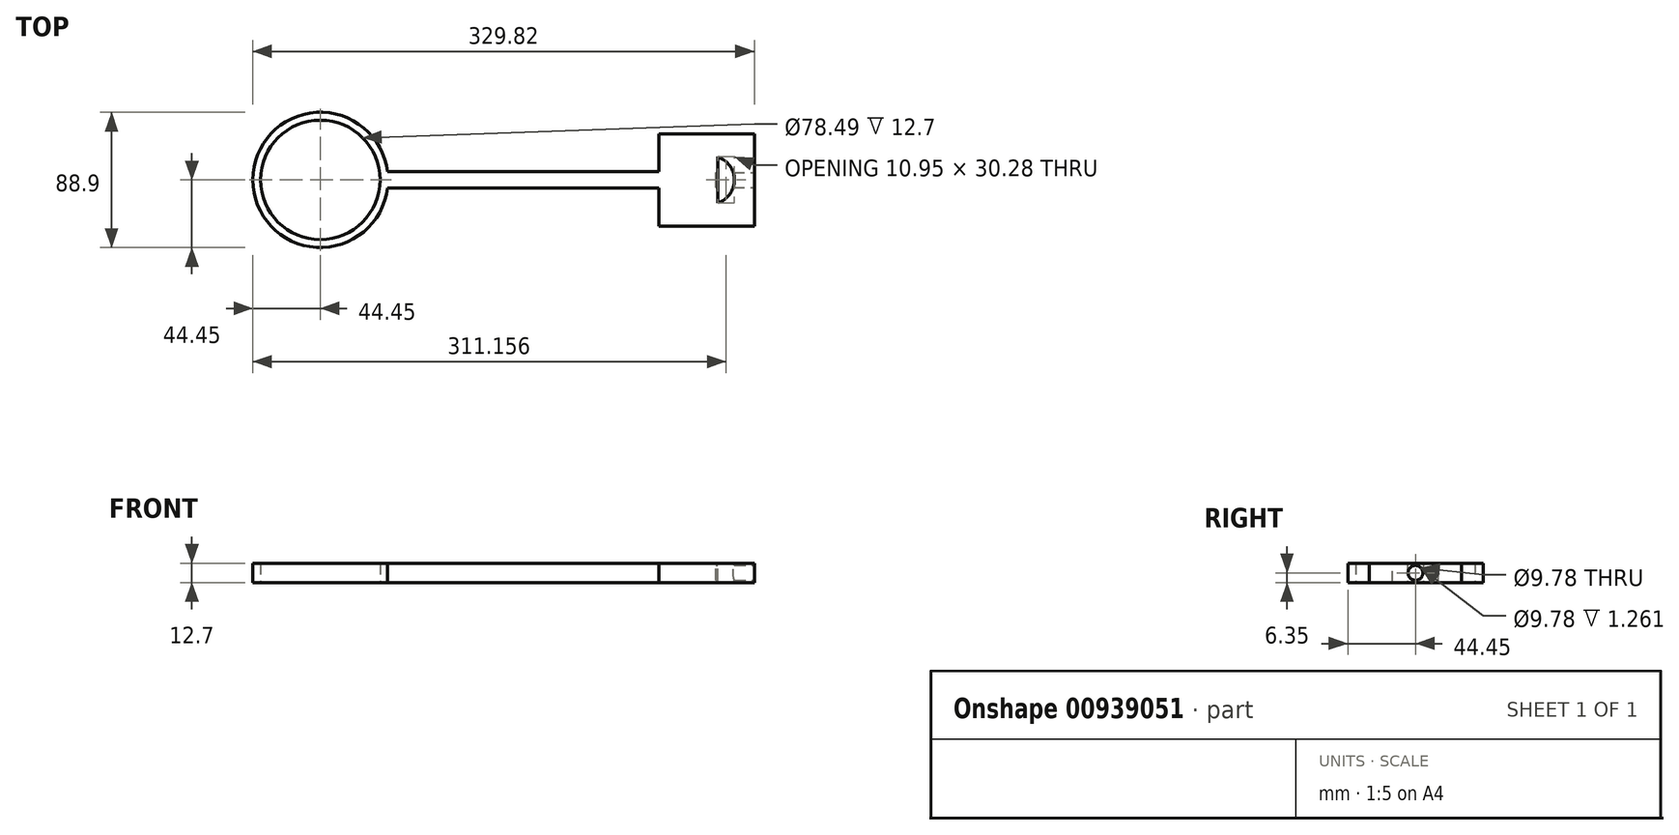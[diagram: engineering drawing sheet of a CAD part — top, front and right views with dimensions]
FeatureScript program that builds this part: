
annotation { "Feature Type Name" : "Feature", "Feature Type Description" : "" }
export const myFeature = defineFeature(function(context is Context, id is Id, definition is map)
    precondition{}
    {
        {
            var Q0;
            Q0=qCreatedBy(makeId("Top.planeOp"),FACE);
            var sketch = newSketch(context, id + "F0", { "sketchPlane" : qUnion([Q0])});
            skLineSegment(sketch, "E0", {"start": v(0, 0) * mm, "end": v(254, 0) * mm});
            skCircle(sketch, "E1", {"center": v(0, 0) * mm, "radius": 39.24 * mm});
            skCircle(sketch, "E2", {"center": v(0, 0) * mm, "radius": 44.45 * mm});
            skLineSegment(sketch, "E3.bottom", {"start": v(285.37, 30.32) * mm, "end": v(222.63, 30.32) * mm});
            skLineSegment(sketch, "E3.top", {"start": v(285.37, -30.32) * mm, "end": v(222.63, -30.32) * mm});
            skLineSegment(sketch, "E3.left", {"start": v(285.37, 30.32) * mm, "end": v(285.37, -30.32) * mm});
            skLineSegment(sketch, "E3.right", {"start": v(222.63, 30.32) * mm, "end": v(222.63, -30.32) * mm});
            skPoint(sketch, "E3.middle", {"position": v(254, 0) * mm});
            skLineSegment(sketch, "E4.bottom", {"start": v(222.63, -5.3) * mm, "end": v(-144.15, -5.3) * mm});
            skLineSegment(sketch, "E4.top", {"start": v(222.63, 5.3) * mm, "end": v(-144.15, 5.3) * mm});
            skLineSegment(sketch, "E4.left", {"start": v(222.63, -5.3) * mm, "end": v(222.63, 5.3) * mm});
            skLineSegment(sketch, "E4.right", {"start": v(-144.15, -5.3) * mm, "end": v(-144.15, 5.3) * mm});
            skPoint(sketch, "E4.middle", {"position": v(39.24, 0) * mm});
            skSolve(sketch);
        }
        {
            var Q0;
            {var subQ3=sQuery(id+"F0.wireOp",EDGE,"E3.bottom");Q0=makeQuery(id+"F0.imprint","IMPRINT",FACE,{"disambiguationData":[TD([[makeQuery(id+"F0.imprint","IMPRINT",EDGE,{"derivedFrom":subQ3}),1.0]])]});}
            var Q1;
            {var subQ0=sQuery(id+"F0.wireOp",EDGE,"E2");var subQ1=sQuery(id+"F0.wireOp",EDGE,"E0");var subQ2=makeQuery(id+"F0.imprint","INTERSECT",VERTEX,{"derivedFrom":[subQ1,subQ0]});Q1=makeQuery(id+"F0.imprint","IMPRINT",FACE,{"disambiguationData":[TD([[makeQuery(id+"F0.imprint","IMPRINT",EDGE,{"disambiguationData":[TD([[subQ2,-1.0]])],"derivedFrom":subQ1}),1.0]])]});}
            var Q2;
            {var subQ0=sQuery(id+"F0.wireOp",EDGE,"E2");var subQ1=sQuery(id+"F0.wireOp",EDGE,"E0");var subQ2=makeQuery(id+"F0.imprint","INTERSECT",VERTEX,{"derivedFrom":[subQ1,subQ0]});Q2=makeQuery(id+"F0.imprint","IMPRINT",FACE,{"disambiguationData":[TD([[makeQuery(id+"F0.imprint","IMPRINT",EDGE,{"disambiguationData":[TD([[subQ2,-1.0]])],"derivedFrom":subQ1}),-1.0]])]});}
            var Q3;
            {var subQ0=sQuery(id+"F0.wireOp",EDGE,"E4.top");var subQ1=sQuery(id+"F0.wireOp",EDGE,"E1");var subQ2=makeQuery(id+"F0.imprint","INTERSECT",VERTEX,{"disambiguationData":[OD(0.0)],"derivedFrom":[subQ1,subQ0]});Q3=makeQuery(id+"F0.imprint","IMPRINT",FACE,{"disambiguationData":[TD([[makeQuery(id+"F0.imprint","IMPRINT",EDGE,{"disambiguationData":[TD([[subQ2,-1.0]])],"derivedFrom":subQ1}),-1.0]])]});}
            var Q4;
            {var subQ0=sQuery(id+"F0.wireOp",EDGE,"E4.bottom");var subQ1=sQuery(id+"F0.wireOp",EDGE,"E1");var subQ2=makeQuery(id+"F0.imprint","INTERSECT",VERTEX,{"disambiguationData":[OD(0.0)],"derivedFrom":[subQ1,subQ0]});Q4=makeQuery(id+"F0.imprint","IMPRINT",FACE,{"disambiguationData":[TD([[makeQuery(id+"F0.imprint","IMPRINT",EDGE,{"disambiguationData":[TD([[subQ2,1.0]])],"derivedFrom":subQ1}),-1.0]])]});}
            var Q5;
            {var subQ0=sQuery(id+"F0.wireOp",EDGE,"E2");var subQ1=sQuery(id+"F0.wireOp",EDGE,"E0");var subQ2=makeQuery(id+"F0.imprint","INTERSECT",VERTEX,{"derivedFrom":[subQ1,subQ0]});Q5=makeQuery(id+"F0.imprint","IMPRINT",FACE,{"disambiguationData":[TD([[makeQuery(id+"F0.imprint","IMPRINT",EDGE,{"disambiguationData":[TD([[subQ2,1.0]])],"derivedFrom":subQ1}),1.0]])]});}
            var Q6;
            {var subQ0=sQuery(id+"F0.wireOp",EDGE,"E2");var subQ1=sQuery(id+"F0.wireOp",EDGE,"E0");var subQ2=makeQuery(id+"F0.imprint","INTERSECT",VERTEX,{"derivedFrom":[subQ1,subQ0]});Q6=makeQuery(id+"F0.imprint","IMPRINT",FACE,{"disambiguationData":[TD([[makeQuery(id+"F0.imprint","IMPRINT",EDGE,{"disambiguationData":[TD([[subQ2,1.0]])],"derivedFrom":subQ1}),-1.0]])]});}
            var Q7;
            {var subQ0=sQuery(id+"F0.wireOp",EDGE,"E4.top");var subQ1=sQuery(id+"F0.wireOp",EDGE,"E1");var subQ2=makeQuery(id+"F0.imprint","INTERSECT",VERTEX,{"disambiguationData":[OD(1.0)],"derivedFrom":[subQ1,subQ0]});Q7=makeQuery(id+"F0.imprint","IMPRINT",FACE,{"disambiguationData":[TD([[makeQuery(id+"F0.imprint","IMPRINT",EDGE,{"disambiguationData":[TD([[subQ2,-1.0]])],"derivedFrom":subQ1}),-1.0]])]});}
            extrude(context, id + "F1", {"entities" : qUnion([Q0, Q1, Q2, Q3, Q4, Q5, Q6, Q7]), "depth" : 12.7 * mm, "offsetDistance" : 25.4 * mm});
        }
        {
            var Q0;
            Q0=makeQuery(id+"F1.opExtrude","CAP_FACE",FACE,{"disambiguationData":[OSD([sQuery(id+"F0.wireOp",EDGE,"E1"),sQuery(id+"F0.wireOp",EDGE,"E2"),sQuery(id+"F0.wireOp",EDGE,"E3.bottom"),sQuery(id+"F0.wireOp",EDGE,"E3.top"),sQuery(id+"F0.wireOp",EDGE,"E3.left"),sQuery(id+"F0.wireOp",EDGE,"E3.right"),sQuery(id+"F0.wireOp",EDGE,"E4.bottom"),sQuery(id+"F0.wireOp",EDGE,"E4.top")])],"isStart":false});
            var sketch = newSketch(context, id + "F2", { "sketchPlane" : qUnion([Q0])});
            skCircle(sketch, "E5", {"center": v(256.24, 0) * mm, "radius": 15.94 * mm});
            skLineSegment(sketch, "E6", {"start": v(261.23, -15.14) * mm, "end": v(261.23, 15.14) * mm});
            skSolve(sketch);
        }
        {
            var Q0;
            {var subQ0=sQuery(id+"F2.wireOp",EDGE,"E6");Q0=makeQuery(id+"F2.imprint","IMPRINT",FACE,{"disambiguationData":[TD([[makeQuery(id+"F2.imprint","IMPRINT",EDGE,{"derivedFrom":subQ0}),-1.0]])]});}
            extrude(context, id + "F3", {"entities" : qUnion([Q0]), "operationType" : NewBodyOperationType.REMOVE, "oppositeDirection" : true, "depth" : 25.4 * mm, "offsetDistance" : 25.4 * mm});
        }
        {
            var Q0;
            Q0=makeQuery(id+"F1.opExtrude","SWEPT_FACE",FACE,{"disambiguationData":[OSD([sQuery(id+"F0.wireOp",EDGE,"E3.left")])]});
            var sketch = newSketch(context, id + "F4", { "sketchPlane" : qUnion([Q0])});
            skCircle(sketch, "E7", {"center": v(0, 6.35) * mm, "radius": 4.89 * mm});
            skPoint(sketch, "E7.centerSnap0", {"position": v(30.32, 6.35) * mm});
            skPoint(sketch, "E7.centerSnap1", {"position": v(0, 0) * mm});
            skSolve(sketch);
        }
        {
            var Q0;
            Q0 = qSketchRegion(id + "F4", true);
            extrude(context, id + "F5", {"entities" : qUnion([Q0]), "operationType" : NewBodyOperationType.REMOVE, "oppositeDirection" : true, "depth" : 25.4 * mm, "offsetDistance" : 25.4 * mm});
        }
    });
